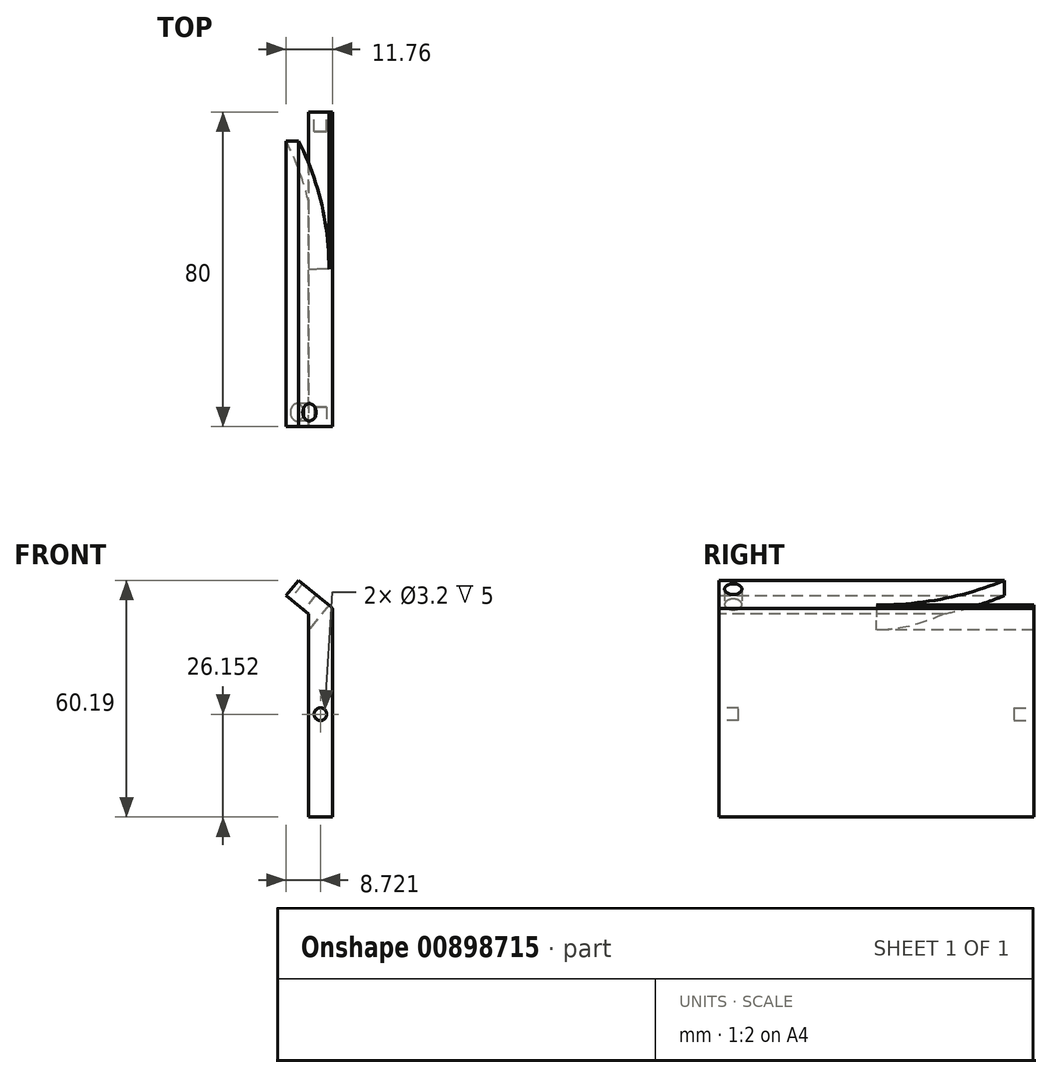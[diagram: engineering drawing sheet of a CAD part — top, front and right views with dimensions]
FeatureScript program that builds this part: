
annotation { "Feature Type Name" : "Feature", "Feature Type Description" : "" }
export const myFeature = defineFeature(function(context is Context, id is Id, definition is map)
    precondition{}
    {
        {
            var Q0;
            Q0=qCreatedBy(makeId("Front.planeOp"),FACE);
            var sketch = newSketch(context, id + "F0", { "sketchPlane" : qUnion([Q0])});
            skLineSegment(sketch, "E0", {"start": v(0, 0) * mm, "end": v(4, 0) * mm});
            skLineSegment(sketch, "E1", {"start": v(4, 0) * mm, "end": v(4, 3) * mm});
            skLineSegment(sketch, "E2", {"start": v(4.23, 3) * mm, "end": v(4, 3) * mm});
            skLineSegment(sketch, "E3", {"start": v(4.23, 3) * mm, "end": v(-4.6, 10.2) * mm});
            skLineSegment(sketch, "E4", {"start": v(-4.6, 10.2) * mm, "end": v(-7.76, 6.31) * mm});
            skLineSegment(sketch, "E5", {"start": v(-7.76, 6.31) * mm, "end": v(0, 0) * mm});
            skSolve(sketch);
        }
        {
            var Q0;
            Q0=makeQuery(id+"F0.imprint","IMPRINT",FACE,{"disambiguationData":[TD([[makeQuery(id+"F0.imprint","IMPRINT",EDGE,{"derivedFrom":sQuery(id+"F0.wireOp",EDGE,"E0")}),1.0]])]});
            extrude(context, id + "F1", {"entities" : qUnion([Q0]), "endBound" : BoundingType.SYMMETRIC, "depth" : 80 * mm, "offsetDistance" : 25 * mm});
        }
        {
            var Q0;
            Q0=makeQuery(id+"F1.opExtrude","SWEPT_FACE",FACE,{"disambiguationData":[OSD([sQuery(id+"F0.wireOp",EDGE,"E0")])]});
            extrude(context, id + "F2", {"entities" : qUnion([Q0]), "operationType" : NewBodyOperationType.ADD, "depth" : 50 * mm, "offsetDistance" : 25 * mm});
        }
        {
            var Q0;
            Q0=makeQuery(id+"F1.opExtrude","SWEPT_FACE",FACE,{"disambiguationData":[OSD([sQuery(id+"F0.wireOp",EDGE,"E5")])]});
            var sketch = newSketch(context, id + "F3", { "sketchPlane" : qUnion([Q0])});
            skCircle(sketch, "E6", {"center": v(-6.4, -36.15) * mm, "radius": 2.2 * mm});
            skCircle(sketch, "E7", {"center": v(-6.4, 36.34) * mm, "radius": 2.2 * mm});
            skCircle(sketch, "E8", {"center": v(-57.9, 0) * mm, "radius": 57.9 * mm});
            skSolve(sketch);
        }
        {
            var Q0;
            {var subQ0=sQuery(id+"F3.wireOp",EDGE,"E8");var subQ1=sQuery(id+"F0.wireOp",EDGE,"E5");var subQ2=makeQuery(id+"F1.opExtrude","SWEPT_EDGE",EDGE,{"disambiguationData":[OSD([sQuery(id+"F0.wireOp",EDGE,"E4"),subQ1])]});var subQ3=makeQuery(id+"F3.imprint","INTERSECT",VERTEX,{"disambiguationData":[OD(0.0)],"derivedFrom":[subQ2,subQ0]});Q0=makeQuery(id+"F3.imprint","IMPRINT",FACE,{"disambiguationData":[TD([[makeQuery(id+"F3.imprint","IMPRINT",EDGE,{"disambiguationData":[TD([[subQ3,-1.0]])],"derivedFrom":subQ2}),1.0]])]});}
            var Q1;
            Q1=makeQuery(id+"F3.imprint","IMPRINT",FACE,{"disambiguationData":[TD([[makeQuery(id+"F3.imprint","IMPRINT",EDGE,{"derivedFrom":sQuery(id+"F3.wireOp",EDGE,"E6")}),1.0]])]});
            var Q2;
            Q2=makeQuery(id+"F3.imprint","IMPRINT",FACE,{"disambiguationData":[TD([[makeQuery(id+"F3.imprint","IMPRINT",EDGE,{"derivedFrom":sQuery(id+"F3.wireOp",EDGE,"E7")}),1.0]])]});
            extrude(context, id + "F4", {"entities" : qUnion([Q0, Q1, Q2]), "operationType" : NewBodyOperationType.REMOVE, "oppositeDirection" : true, "depth" : 28.8 * mm, "offsetDistance" : 25 * mm, "hasSecondDirection" : true, "secondDirectionOppositeDirection" : false, "secondDirectionDepth" : 25 * mm});
        }
        {
            var Q0;
            Q0=makeQuery(id+"F2.opExtrude","CAP_FACE",FACE,{"disambiguationData":[OSD([sQuery(id+"F0.wireOp",EDGE,"E0")])],"isStart":false});
            var sketch = newSketch(context, id + "F5", { "sketchPlane" : qUnion([Q0])});
            skLineSegment(sketch, "E9.bottom", {"start": v(14.56, -40) * mm, "end": v(4.36, -40) * mm});
            skLineSegment(sketch, "E9.top", {"start": v(14.56, 40) * mm, "end": v(4.36, 40) * mm});
            skLineSegment(sketch, "E9.left", {"start": v(14.56, -40) * mm, "end": v(14.56, 40) * mm});
            skLineSegment(sketch, "E9.right", {"start": v(4.36, -40) * mm, "end": v(4.36, 40) * mm});
            skSolve(sketch);
        }
        {
            var Q0;
            Q0=qSketchRegion(id+"F5",true);
            var Q1;
            {var subQ0=sQuery(id+"F5.wireOp",EDGE,"E9.left");var subQ1=sQuery(id+"F0.wireOp",EDGE,"E0");var subQ2=makeQuery(id+"F2.opExtrude","CAP_EDGE",EDGE,{"disambiguationData":[OSD([subQ1]),TDD([makeQuery(id+"F1.opExtrude","CAP_EDGE",EDGE,{"disambiguationData":[OSD([subQ1])],"isStart":true})])],"isStart":false});var subQ3=makeQuery(id+"F5.imprint","INTERSECT",VERTEX,{"derivedFrom":[subQ2,subQ0]});Q1=makeQuery(id+"F5.imprint","IMPRINT",FACE,{"disambiguationData":[TD([[makeQuery(id+"F5.imprint","IMPRINT",EDGE,{"disambiguationData":[TD([[subQ3,-1.0]])],"derivedFrom":subQ0}),1.0]])]});}
            extrude(context, id + "F6", {"entities" : qUnion([Q0, Q1]), "operationType" : NewBodyOperationType.REMOVE, "oppositeDirection" : true, "depth" : 24.9 * mm, "offsetDistance" : 25 * mm});
        }
        {
            var Q0;
            Q0=makeQuery(id+"F1.opExtrude","SWEPT_EDGE",EDGE,{"disambiguationData":[OSD([sQuery(id+"F0.wireOp",EDGE,"E2"),sQuery(id+"F0.wireOp",EDGE,"E3")])]});
            fillet(context, id + "F7", {"entities" : qUnion([Q0]), "radius" : 3 * mm, "tangentPropagation" : true, "allowEdgeOverflow" : false});
        }
        {
            var Q0;
            Q0=makeQuery(id+"F2.opExtrude","SWEPT_FACE",FACE,{"disambiguationData":[OSD([sQuery(id+"F0.wireOp",EDGE,"E0"),sQuery(id+"F0.wireOp",EDGE,"E5")])]});
            var sketch = newSketch(context, id + "F8", { "sketchPlane" : qUnion([Q0])});
            skLineSegment(sketch, "E10.bottom", {"start": v(-40, 0) * mm, "end": v(40, 0) * mm});
            skLineSegment(sketch, "E10.top", {"start": v(-40, -50) * mm, "end": v(40, -50) * mm});
            skLineSegment(sketch, "E10.left", {"start": v(-40, 0) * mm, "end": v(-40, -50) * mm});
            skLineSegment(sketch, "E10.right", {"start": v(40, 0) * mm, "end": v(40, -50) * mm});
            skSolve(sketch);
        }
        {
            var Q0;
            Q0=qSketchRegion(id+"F8",true);
            var Q1;
            Q1=makeQuery(id+"F8.imprint","IMPRINT",FACE,{"disambiguationData":[TD([[makeQuery(id+"F8.imprint","IMPRINT",EDGE,{"derivedFrom":sQuery(id+"F8.wireOp",EDGE,"E10.top")}),-1.0]])]});
            extrude(context, id + "F9", {"entities" : qUnion([Q0, Q1]), "operationType" : NewBodyOperationType.ADD, "depth" : 2 * mm, "offsetDistance" : 25 * mm});
        }
        {
            var Q0;
            {var subQ0=sQuery(id+"F0.wireOp",EDGE,"E0");Q0=makeQuery(id+"F9.boolean.opBoolean","MERGE",FACE,{"derivedFrom":[makeQuery(id+"F2.boolean.opBoolean","MERGE",FACE,{"derivedFrom":[makeQuery(id+"F1.opExtrude","CAP_FACE",FACE,{"disambiguationData":[OSD([subQ0,sQuery(id+"F0.wireOp",EDGE,"E1"),sQuery(id+"F0.wireOp",EDGE,"E2"),sQuery(id+"F0.wireOp",EDGE,"E3"),sQuery(id+"F0.wireOp",EDGE,"E4"),sQuery(id+"F0.wireOp",EDGE,"E5")])],"isStart":false}),makeQuery(id+"F2.opExtrude","SWEPT_FACE",FACE,{"disambiguationData":[OSD([subQ0]),TDD([makeQuery(id+"F1.opExtrude","CAP_EDGE",EDGE,{"disambiguationData":[OSD([subQ0])],"isStart":false})])]})]}),makeQuery(id+"F9.opExtrude","SWEPT_FACE",FACE,{"disambiguationData":[OSD([sQuery(id+"F8.wireOp",EDGE,"E10.right")])]})]});}
            var sketch = newSketch(context, id + "F10", { "sketchPlane" : qUnion([Q0])});
            skLineSegment(sketch, "E11", {"start": v(-2, 0) * mm, "end": v(-2, 1.63) * mm});
            skSolve(sketch);
        }
        {
            var Q0;
            Q0 = qSketchRegion(id + "F10", true);
            var Q1;
            {var subQ0=sQuery(id+"F10.wireOp",EDGE,"E11");Q1=makeQuery(id+"F10.imprint","IMPRINT",FACE,{"disambiguationData":[TD([[makeQuery(id+"F10.imprint","IMPRINT",EDGE,{"derivedFrom":subQ0}),-1.0]])]});}
            extrude(context, id + "F11", {"entities" : qUnion([Q0, Q1]), "oppositeDirection" : true, "depth" : 80 * mm, "offsetDistance" : 25 * mm});
        }
        {
            var Q0;
            Q0=makeQuery(id+"F1.opExtrude","SWEPT_BODY",BODY,{"disambiguationData":[OSD([sQuery(id+"F0.wireOp",EDGE,"E0"),sQuery(id+"F0.wireOp",EDGE,"E1"),sQuery(id+"F0.wireOp",EDGE,"E2"),sQuery(id+"F0.wireOp",EDGE,"E3"),sQuery(id+"F0.wireOp",EDGE,"E4"),sQuery(id+"F0.wireOp",EDGE,"E5")])]});
            var Q1;
            Q1=makeQuery(id+"F11.opExtrude","SWEPT_BODY",BODY,{"disambiguationData":[OSD([sQuery(id+"F0.wireOp",EDGE,"E5"),sQuery(id+"F8.wireOp",EDGE,"E10.bottom"),sQuery(id+"F8.wireOp",EDGE,"E10.right"),sQuery(id+"F10.wireOp",EDGE,"E11")])]});
            booleanBodies(context, id + "F12", {"operationType" : BooleanOperationType.UNION, "tools" : qUnion([Q0, Q1])});
        }
        {
            var Q0;
            Q0=makeQuery(id+"F11.opExtrude","SWEPT_FACE",FACE,{"disambiguationData":[OSD([sQuery(id+"F0.wireOp",EDGE,"E5")])]});
            extrude(context, id + "F13", {"entities" : qUnion([Q0]), "operationType" : NewBodyOperationType.REMOVE, "oppositeDirection" : true, "depth" : 25 * mm, "offsetDistance" : 25 * mm});
        }
        {
            var Q0;
            {var subQ0=sQuery(id+"F0.wireOp",EDGE,"E5");var subQ1=sQuery(id+"F0.wireOp",EDGE,"E0");Q0=makeQuery(id+"F12.opBoolean","MERGE",FACE,{"derivedFrom":[makeQuery(id+"F9.boolean.opBoolean","MERGE",FACE,{"derivedFrom":[makeQuery(id+"F2.boolean.opBoolean","MERGE",FACE,{"derivedFrom":[makeQuery(id+"F1.opExtrude","CAP_FACE",FACE,{"disambiguationData":[OSD([subQ1,sQuery(id+"F0.wireOp",EDGE,"E1"),sQuery(id+"F0.wireOp",EDGE,"E2"),sQuery(id+"F0.wireOp",EDGE,"E3"),sQuery(id+"F0.wireOp",EDGE,"E4"),subQ0])],"isStart":true}),makeQuery(id+"F2.opExtrude","SWEPT_FACE",FACE,{"disambiguationData":[OSD([subQ1]),TDD([makeQuery(id+"F1.opExtrude","CAP_EDGE",EDGE,{"disambiguationData":[OSD([subQ1])],"isStart":true})])]})]}),makeQuery(id+"F9.opExtrude","SWEPT_FACE",FACE,{"disambiguationData":[OSD([sQuery(id+"F8.wireOp",EDGE,"E10.left")])]})]}),makeQuery(id+"F11.opExtrude","CAP_FACE",FACE,{"disambiguationData":[OSD([subQ0,sQuery(id+"F8.wireOp",EDGE,"E10.bottom"),sQuery(id+"F8.wireOp",EDGE,"E10.right"),sQuery(id+"F10.wireOp",EDGE,"E11")])],"isStart":false})]});}
            var sketch = newSketch(context, id + "F14", { "sketchPlane" : qUnion([Q0])});
            skLineSegment(sketch, "E12", {"start": v(-4, 3) * mm, "end": v(2, 1.63) * mm});
            skCircle(sketch, "E13", {"center": v(-0.96, -23.85) * mm, "radius": 1.6 * mm});
            skSolve(sketch);
        }
        {
            var Q0;
            Q0 = qSketchRegion(id + "F14", true);
            var Q1;
            Q1=makeQuery(id+"F14.imprint","IMPRINT",FACE,{"disambiguationData":[TD([[makeQuery(id+"F14.imprint","IMPRINT",EDGE,{"derivedFrom":sQuery(id+"F14.wireOp",EDGE,"E13")}),1.0]])]});
            extrude(context, id + "F15", {"entities" : qUnion([Q0, Q1]), "operationType" : NewBodyOperationType.REMOVE, "oppositeDirection" : true, "depth" : 5 * mm, "offsetDistance" : 25 * mm});
        }
        {
            var Q0;
            {var subQ0=sQuery(id+"F8.wireOp",EDGE,"E10.right");var subQ1=sQuery(id+"F0.wireOp",EDGE,"E5");var subQ2=sQuery(id+"F0.wireOp",EDGE,"E0");Q0=makeQuery(id+"F12.opBoolean","MERGE",FACE,{"derivedFrom":[makeQuery(id+"F9.boolean.opBoolean","MERGE",FACE,{"derivedFrom":[makeQuery(id+"F2.boolean.opBoolean","MERGE",FACE,{"derivedFrom":[makeQuery(id+"F1.opExtrude","CAP_FACE",FACE,{"disambiguationData":[OSD([subQ2,sQuery(id+"F0.wireOp",EDGE,"E1"),sQuery(id+"F0.wireOp",EDGE,"E2"),sQuery(id+"F0.wireOp",EDGE,"E3"),sQuery(id+"F0.wireOp",EDGE,"E4"),subQ1])],"isStart":false}),makeQuery(id+"F2.opExtrude","SWEPT_FACE",FACE,{"disambiguationData":[OSD([subQ2]),TDD([makeQuery(id+"F1.opExtrude","CAP_EDGE",EDGE,{"disambiguationData":[OSD([subQ2])],"isStart":false})])]})]}),makeQuery(id+"F9.opExtrude","SWEPT_FACE",FACE,{"disambiguationData":[OSD([subQ0])]})]}),makeQuery(id+"F11.opExtrude","CAP_FACE",FACE,{"disambiguationData":[OSD([subQ1,sQuery(id+"F8.wireOp",EDGE,"E10.bottom"),subQ0,sQuery(id+"F10.wireOp",EDGE,"E11")])],"isStart":true})]});}
            var sketch = newSketch(context, id + "F16", { "sketchPlane" : qUnion([Q0])});
            skLineSegment(sketch, "E14", {"start": v(4, -50) * mm, "end": v(4, 3) * mm});
            skCircle(sketch, "E15", {"center": v(0.96, -23.85) * mm, "radius": 1.6 * mm});
            skSolve(sketch);
        }
        {
            var Q0;
            Q0=makeQuery(id+"F16.imprint","IMPRINT",FACE,{"disambiguationData":[TD([[makeQuery(id+"F16.imprint","IMPRINT",EDGE,{"derivedFrom":sQuery(id+"F16.wireOp",EDGE,"E15")}),1.0]])]});
            extrude(context, id + "F17", {"entities" : qUnion([Q0]), "operationType" : NewBodyOperationType.REMOVE, "oppositeDirection" : true, "depth" : 5 * mm, "offsetDistance" : 25 * mm});
        }
    });
